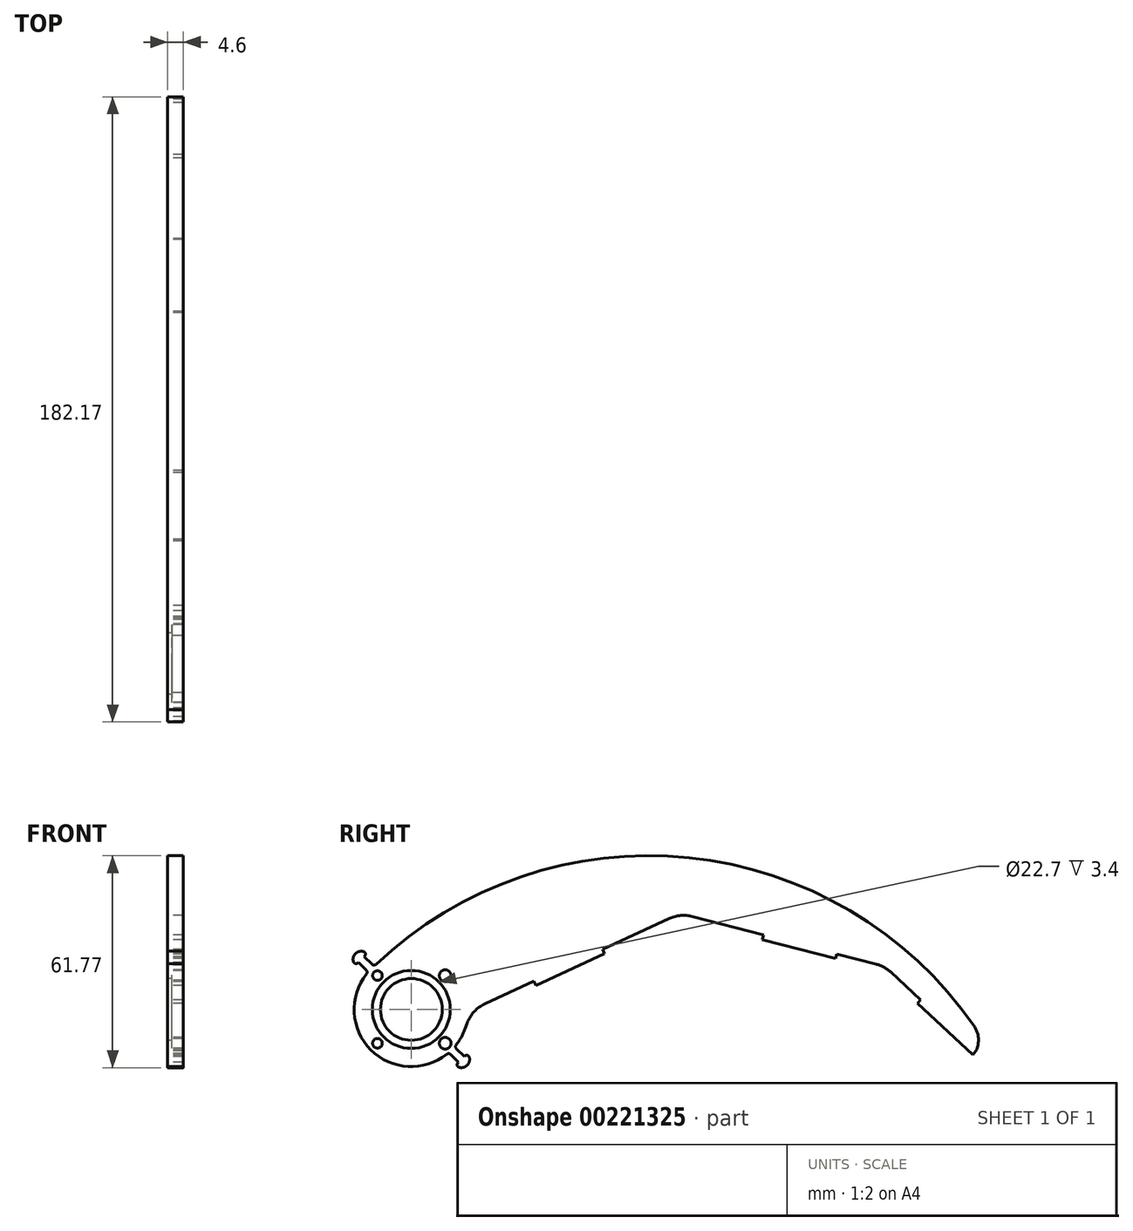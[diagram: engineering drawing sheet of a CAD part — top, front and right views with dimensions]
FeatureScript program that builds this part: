
annotation { "Feature Type Name" : "Feature", "Feature Type Description" : "" }
export const myFeature = defineFeature(function(context is Context, id is Id, definition is map)
    precondition{}
    {
        {
            var Q0;
            Q0=qCreatedBy(makeId("Right.planeOp"),FACE);
            var sketch = newSketch(context, id + "F0", { "sketchPlane" : qUnion([Q0])});
            skCircle(sketch, "E0", {"center": v(0, 0) * mm, "radius": 200 * mm, "construction": true});
            skCircle(sketch, "E1", {"center": v(0, 0) * mm, "radius": 9 * mm});
            skCircle(sketch, "E2", {"center": v(143.28, 0) * mm, "radius": 13 * mm, "construction": true});
            skCircle(sketch, "E3.1.0.0", {"center": v(200, 0) * mm, "radius": 200 * mm, "construction": true});
            skLineSegment(sketch, "E3.direction1", {"start": v(0, 0) * mm, "end": v(200, 0) * mm, "construction": true});
            skLineSegment(sketch, "E4", {"start": v(200, 0) * mm, "end": v(5.32, 45.84) * mm, "construction": true});
            skCircle(sketch, "E5", {"center": v(178.19, 0) * mm, "radius": 5 * mm, "construction": true});
            skCircle(sketch, "E6", {"center": v(108.38, 0) * mm, "radius": 21 * mm, "construction": true});
            skCircle(sketch, "E7", {"center": v(51.66, 0) * mm, "radius": 34 * mm, "construction": true});
            skCircle(sketch, "E8", {"center": v(0, 0) * mm, "radius": 13.95 * mm, "construction": true});
            skLineSegment(sketch, "E9", {"start": v(0, 0) * mm, "end": v(-9.86, 9.86) * mm, "construction": true});
            skCircle(sketch, "E10", {"center": v(-9.86, 9.86) * mm, "radius": 1.4 * mm});
            skCircle(sketch, "E11", {"center": v(0, 0) * mm, "radius": 11.25 * mm, "construction": true});
            skLineSegment(sketch, "E12", {"start": v(143.28, 0) * mm, "end": v(160.73, -17.45) * mm, "construction": true});
            skLineSegment(sketch, "E13", {"start": v(160.73, -17.45) * mm, "end": v(178.19, 0) * mm, "construction": true});
            skLineSegment(sketch, "E14", {"start": v(160.73, -17.45) * mm, "end": v(160.73, 0) * mm, "construction": true});
            skCircle(sketch, "E15.cCircle", {"center": v(88, -78.54) * mm, "radius": 100 * mm, "construction": true});
            skPoint(sketch, "E15.0.midPoint", {"position": v(88, 21.46) * mm});
            skLineSegment(sketch, "E16.bottom", {"start": v(56.28, 16.2) * mm, "end": v(36.32, 6.96) * mm});
            skLineSegment(sketch, "E16.top", {"start": v(55.7, 17.47) * mm, "end": v(35.73, 8.23) * mm, "construction": true});
            skLineSegment(sketch, "E16.left", {"start": v(56.28, 16.2) * mm, "end": v(55.7, 17.47) * mm});
            skLineSegment(sketch, "E16.right", {"start": v(36.32, 6.96) * mm, "end": v(35.73, 8.23) * mm});
            skPoint(sketch, "E16.middle", {"position": v(46, 12.22) * mm});
            skLineSegment(sketch, "E17", {"start": v(113.11, 18.26) * mm, "end": v(88, -78.54) * mm, "construction": true});
            skLineSegment(sketch, "E18", {"start": v(46, 12.22) * mm, "end": v(88, -78.54) * mm, "construction": true});
            skLineSegment(sketch, "E19.bottom", {"start": v(123.59, 14.82) * mm, "end": v(102.3, 20.34) * mm});
            skLineSegment(sketch, "E19.top", {"start": v(123.94, 16.17) * mm, "end": v(102.64, 21.7) * mm, "construction": true});
            skLineSegment(sketch, "E19.left", {"start": v(123.59, 14.82) * mm, "end": v(123.94, 16.17) * mm});
            skLineSegment(sketch, "E19.right", {"start": v(102.3, 20.34) * mm, "end": v(102.64, 21.7) * mm});
            skPoint(sketch, "E19.middle", {"position": v(113.11, 18.26) * mm});
            skLineSegment(sketch, "E20.bottom", {"start": v(164.5, -12.13) * mm, "end": v(163.54, -13.15) * mm});
            skLineSegment(sketch, "E20.top", {"start": v(148.35, 2.82) * mm, "end": v(147.4, 1.8) * mm});
            skLineSegment(sketch, "E20.left", {"start": v(164.5, -12.13) * mm, "end": v(148.35, 2.82) * mm, "construction": true});
            skLineSegment(sketch, "E20.right", {"start": v(163.54, -13.15) * mm, "end": v(147.4, 1.8) * mm});
            skPoint(sketch, "E20.middle", {"position": v(155.95, -5.17) * mm});
            skLineSegment(sketch, "E21", {"start": v(155.95, -5.17) * mm, "end": v(88, -78.54) * mm, "construction": true});
            skCircle(sketch, "E22", {"center": v(88, -78.54) * mm, "radius": 101.3 * mm, "construction": true});
            skCircle(sketch, "E23", {"center": v(160.83, -8.73) * mm, "radius": 5 * mm, "construction": true});
            skArc(sketch, "E24", {"start": v(163.89, -4.78) * mm, "mid": v(165.18, -8.37) * mm, "end": v(164.5, -12.13) * mm});
            skLineSegment(sketch, "E25", {"start": v(102.64, 21.7) * mm, "end": v(81.88, 27.09) * mm});
            skLineSegment(sketch, "E26", {"start": v(75.16, 26.48) * mm, "end": v(55.7, 17.47) * mm});
            skLineSegment(sketch, "E27", {"start": v(35.73, 8.23) * mm, "end": v(21.44, 1.62) * mm});
            skLineSegment(sketch, "E28", {"start": v(16.24, -4.05) * mm, "end": v(15.66, -5.66) * mm});
            skLineSegment(sketch, "E29", {"start": v(123.94, 16.17) * mm, "end": v(135.39, 13.2) * mm});
            skLineSegment(sketch, "E30", {"start": v(139.67, 10.86) * mm, "end": v(148.35, 2.82) * mm});
            skPoint(sketch, "E31.visualSharp", {"position": v(137.83, 12.57) * mm});
            skArc(sketch, "E31.filletArc", {"start": v(139.67, 10.86) * mm, "mid": v(137.68, 12.3) * mm, "end": v(135.39, 13.2) * mm});
            skPoint(sketch, "E32.visualSharp", {"position": v(78.41, 27.99) * mm});
            skArc(sketch, "E32.filletArc", {"start": v(81.88, 27.09) * mm, "mid": v(78.47, 27.37) * mm, "end": v(75.16, 26.48) * mm});
            skPoint(sketch, "E33.visualSharp", {"position": v(17.66, -0.13) * mm});
            skArc(sketch, "E33.filletArc", {"start": v(21.44, 1.62) * mm, "mid": v(18.27, -0.7) * mm, "end": v(16.24, -4.05) * mm});
            skCircle(sketch, "E34.1.0", {"center": v(-9.86, -9.86) * mm, "radius": 1.4 * mm});
            skCircle(sketch, "E34.2.0", {"center": v(9.86, -9.86) * mm, "radius": 1.4 * mm, "construction": true});
            skCircle(sketch, "E34.3.0", {"center": v(9.86, 9.86) * mm, "radius": 1.4 * mm, "construction": true});
            skCircle(sketch, "E35", {"center": v(0, 0) * mm, "radius": 21.25 * mm, "construction": true});
            skLineSegment(sketch, "E36", {"start": v(0, 0) * mm, "end": v(0, -17.25) * mm, "construction": true});
            skCircle(sketch, "E37", {"center": v(-9.86, -9.86) * mm, "radius": 2.7 * mm, "construction": true});
            skPoint(sketch, "E38.orphan", {"position": v(-2.72, -20.18) * mm});
            skCircle(sketch, "E39", {"center": v(9.86, 9.86) * mm, "radius": 1.7 * mm});
            skCircle(sketch, "E40", {"center": v(9.86, -9.86) * mm, "radius": 1.7 * mm});
            skArc(sketch, "E41", {"start": v(-12.6, 10.9) * mm, "mid": v(-11.77, -11.77) * mm, "end": v(10.9, -12.6) * mm});
            skLineSegment(sketch, "E42.bottom", {"start": v(-13.72, 15.42) * mm, "end": v(-10.9, 12.6) * mm});
            skLineSegment(sketch, "E42.top", {"start": v(-15.42, 13.72) * mm, "end": v(-12.6, 10.9) * mm});
            skLineSegment(sketch, "E42.left", {"start": v(-13.72, 15.42) * mm, "end": v(-15.42, 13.72) * mm, "construction": true});
            skLineSegment(sketch, "E43", {"start": v(-14.57, 14.57) * mm, "end": v(-11.74, 11.74) * mm, "construction": true});
            skArc(sketch, "E44", {"start": v(-12.87, 16.27) * mm, "mid": v(-16.27, 16.27) * mm, "end": v(-16.27, 12.87) * mm});
            skLineSegment(sketch, "E45", {"start": v(-13.72, 15.42) * mm, "end": v(-12.87, 16.27) * mm});
            skLineSegment(sketch, "E46", {"start": v(-15.42, 13.72) * mm, "end": v(-16.27, 12.87) * mm});
            skLineSegment(sketch, "E47", {"start": v(0, 0) * mm, "end": v(9.86, 9.86) * mm, "construction": true});
            skLineSegment(sketch, "E48.MirrorCS", {"start": v(15.42, -13.72) * mm, "end": v(12.6, -10.9) * mm});
            skLineSegment(sketch, "E49.MirrorCS", {"start": v(15.42, -13.72) * mm, "end": v(16.27, -12.87) * mm});
            skArc(sketch, "E50.MirrorCS", {"start": v(16.27, -12.87) * mm, "mid": v(16.27, -16.27) * mm, "end": v(12.87, -16.27) * mm});
            skLineSegment(sketch, "E51.MirrorCS", {"start": v(13.72, -15.42) * mm, "end": v(12.87, -16.27) * mm});
            skLineSegment(sketch, "E52.MirrorCS", {"start": v(13.72, -15.42) * mm, "end": v(10.9, -12.6) * mm});
            skArc(sketch, "E53.trimOffspring", {"start": v(12.6, -10.9) * mm, "mid": v(14.37, -8.42) * mm, "end": v(15.66, -5.66) * mm});
            skArc(sketch, "E54", {"start": v(163.89, -4.78) * mm, "mid": v(80.5, 44.24) * mm, "end": v(-10.9, 12.6) * mm});
            skLineSegment(sketch, "E55", {"start": v(0, 0) * mm, "end": v(26.66, -57.6) * mm, "construction": true});
            skLineSegment(sketch, "E56", {"start": v(0, 0) * mm, "end": v(-15.25, -58.78) * mm, "construction": true});
            skLineSegment(sketch, "E57", {"start": v(0, 0) * mm, "end": v(-37.75, -40.76) * mm, "construction": true});
            skSolve(sketch);
        }
        {
            var Q0;
            Q0 = qSketchRegion(id + "F0", true);
            extrude(context, id + "F1", {"entities" : qUnion([Q0]), "depth" : 1.2 * mm});
        }
        {
            var Q0;
            Q0=makeQuery(id+"F1.opExtrude","CAP_FACE",FACE,{"disambiguationData":[OSD([sQuery(id+"F0.wireOp",EDGE,"E1"),sQuery(id+"F0.wireOp",EDGE,"E10"),sQuery(id+"F0.wireOp",EDGE,"E16.bottom"),sQuery(id+"F0.wireOp",EDGE,"E16.left"),sQuery(id+"F0.wireOp",EDGE,"E16.right"),sQuery(id+"F0.wireOp",EDGE,"E19.bottom"),sQuery(id+"F0.wireOp",EDGE,"E19.left"),sQuery(id+"F0.wireOp",EDGE,"E19.right"),sQuery(id+"F0.wireOp",EDGE,"E20.bottom"),sQuery(id+"F0.wireOp",EDGE,"E20.top"),sQuery(id+"F0.wireOp",EDGE,"E20.right"),sQuery(id+"F0.wireOp",EDGE,"E24"),sQuery(id+"F0.wireOp",EDGE,"E25"),sQuery(id+"F0.wireOp",EDGE,"E26"),sQuery(id+"F0.wireOp",EDGE,"E27"),sQuery(id+"F0.wireOp",EDGE,"E28"),sQuery(id+"F0.wireOp",EDGE,"E29"),sQuery(id+"F0.wireOp",EDGE,"E30"),sQuery(id+"F0.wireOp",EDGE,"E31.filletArc"),sQuery(id+"F0.wireOp",EDGE,"E32.filletArc"),sQuery(id+"F0.wireOp",EDGE,"E33.filletArc"),sQuery(id+"F0.wireOp",EDGE,"E34.1.0"),sQuery(id+"F0.wireOp",EDGE,"E39"),sQuery(id+"F0.wireOp",EDGE,"E40"),sQuery(id+"F0.wireOp",EDGE,"E41"),sQuery(id+"F0.wireOp",EDGE,"E42.bottom"),sQuery(id+"F0.wireOp",EDGE,"E42.top"),sQuery(id+"F0.wireOp",EDGE,"E44"),sQuery(id+"F0.wireOp",EDGE,"E45"),sQuery(id+"F0.wireOp",EDGE,"E46"),sQuery(id+"F0.wireOp",EDGE,"E48.MirrorCS"),sQuery(id+"F0.wireOp",EDGE,"E49.MirrorCS"),sQuery(id+"F0.wireOp",EDGE,"E50.MirrorCS"),sQuery(id+"F0.wireOp",EDGE,"E51.MirrorCS"),sQuery(id+"F0.wireOp",EDGE,"E52.MirrorCS"),sQuery(id+"F0.wireOp",EDGE,"E53.trimOffspring"),sQuery(id+"F0.wireOp",EDGE,"E54")])],"isStart":false});
            var sketch = newSketch(context, id + "F2", { "sketchPlane" : qUnion([Q0])});
            skLineSegment(sketch, "E58.0", {"start": v(123.59, 14.82) * mm, "end": v(102.3, 20.34) * mm});
            skPoint(sketch, "E59.0", {"position": v(78.47, 27.37) * mm});
            skArc(sketch, "E59.1", {"start": v(81.88, 27.09) * mm, "mid": v(78.47, 27.37) * mm, "end": v(75.16, 26.48) * mm});
            skLineSegment(sketch, "E60.0", {"start": v(102.64, 21.7) * mm, "end": v(81.88, 27.09) * mm});
            skLineSegment(sketch, "E61.0", {"start": v(123.94, 16.17) * mm, "end": v(135.39, 13.2) * mm});
            skArc(sketch, "E62.0", {"start": v(139.67, 10.86) * mm, "mid": v(137.68, 12.3) * mm, "end": v(135.39, 13.2) * mm});
            skLineSegment(sketch, "E63.0", {"start": v(139.67, 10.86) * mm, "end": v(148.35, 2.82) * mm});
            skLineSegment(sketch, "E64.0", {"start": v(163.54, -13.15) * mm, "end": v(147.4, 1.8) * mm});
            skArc(sketch, "E65.0", {"start": v(163.89, -4.78) * mm, "mid": v(165.18, -8.37) * mm, "end": v(164.5, -12.13) * mm});
            skArc(sketch, "E66.0", {"start": v(163.89, -4.78) * mm, "mid": v(80.5, 44.24) * mm, "end": v(-10.9, 12.6) * mm});
            skLineSegment(sketch, "E67.0", {"start": v(75.16, 26.48) * mm, "end": v(55.7, 17.47) * mm});
            skLineSegment(sketch, "E68.0", {"start": v(56.28, 16.2) * mm, "end": v(36.32, 6.96) * mm});
            skArc(sketch, "E69.0", {"start": v(21.44, 1.62) * mm, "mid": v(18.27, -0.7) * mm, "end": v(16.24, -4.05) * mm});
            skLineSegment(sketch, "E70.0", {"start": v(16.24, -4.05) * mm, "end": v(15.66, -5.66) * mm});
            skArc(sketch, "E71.0", {"start": v(12.6, -10.9) * mm, "mid": v(14.37, -8.42) * mm, "end": v(15.66, -5.66) * mm});
            skLineSegment(sketch, "E72.0", {"start": v(15.42, -13.72) * mm, "end": v(12.6, -10.9) * mm});
            skLineSegment(sketch, "E73.0", {"start": v(13.72, -15.42) * mm, "end": v(10.9, -12.6) * mm});
            skCircle(sketch, "E74.0", {"center": v(9.86, -9.86) * mm, "radius": 1.7 * mm});
            skArc(sketch, "E75.0", {"start": v(-12.6, 10.9) * mm, "mid": v(-11.77, -11.77) * mm, "end": v(10.9, -12.6) * mm});
            skCircle(sketch, "E76.0", {"center": v(-9.86, -9.86) * mm, "radius": 1.4 * mm});
            skCircle(sketch, "E77.0", {"center": v(-9.86, 9.86) * mm, "radius": 1.4 * mm});
            skCircle(sketch, "E78.0", {"center": v(9.86, 9.86) * mm, "radius": 1.7 * mm});
            skLineSegment(sketch, "E79.0", {"start": v(-15.42, 13.72) * mm, "end": v(-12.6, 10.9) * mm});
            skLineSegment(sketch, "E80.0", {"start": v(-13.72, 15.42) * mm, "end": v(-10.9, 12.6) * mm});
            skArc(sketch, "E81.0", {"start": v(16.27, -12.87) * mm, "mid": v(16.27, -16.27) * mm, "end": v(12.87, -16.27) * mm});
            skArc(sketch, "E82.0", {"start": v(-12.87, 16.27) * mm, "mid": v(-16.27, 16.27) * mm, "end": v(-16.27, 12.87) * mm});
            skLineSegment(sketch, "E83", {"start": v(15.42, -13.72) * mm, "end": v(16.27, -12.87) * mm});
            skLineSegment(sketch, "E84", {"start": v(13.72, -15.42) * mm, "end": v(12.87, -16.27) * mm});
            skLineSegment(sketch, "E85", {"start": v(21.44, 1.62) * mm, "end": v(35.73, 8.23) * mm});
            skLineSegment(sketch, "E86", {"start": v(35.73, 8.23) * mm, "end": v(36.32, 6.96) * mm});
            skCircle(sketch, "E87", {"center": v(0, 0) * mm, "radius": 11.35 * mm});
            skLineSegment(sketch, "E88", {"start": v(-16.27, 12.87) * mm, "end": v(-15.42, 13.72) * mm});
            skLineSegment(sketch, "E89", {"start": v(-13.72, 15.42) * mm, "end": v(-12.87, 16.27) * mm});
            skLineSegment(sketch, "E90", {"start": v(55.7, 17.47) * mm, "end": v(56.28, 16.2) * mm});
            skLineSegment(sketch, "E91", {"start": v(102.64, 21.7) * mm, "end": v(102.3, 20.34) * mm});
            skLineSegment(sketch, "E92", {"start": v(123.59, 14.82) * mm, "end": v(123.94, 16.17) * mm});
            skLineSegment(sketch, "E93", {"start": v(148.35, 2.82) * mm, "end": v(147.4, 1.8) * mm});
            skLineSegment(sketch, "E94", {"start": v(163.54, -13.15) * mm, "end": v(164.5, -12.13) * mm});
            skCircle(sketch, "E95", {"center": v(0, 0) * mm, "radius": 9 * mm});
            skCircle(sketch, "E96", {"center": v(0, 0) * mm, "radius": 9.4 * mm});
            skSolve(sketch);
        }
        {
            var Q0;
            Q0 = qSketchRegion(id + "F2", true);
            extrude(context, id + "F3", {"entities" : qUnion([Q0]), "operationType" : NewBodyOperationType.ADD, "depth" : 3.4 * mm});
        }
        {
            var Q0;
            Q0=makeQuery(id+"F3.boolean.opBoolean","MERGE",EDGE,{"derivedFrom":[makeQuery(id+"F1.opExtrude","SWEPT_EDGE",EDGE,{"disambiguationData":[OSD([sQuery(id+"F0.wireOp",EDGE,"E50.MirrorCS"),sQuery(id+"F0.wireOp",EDGE,"E51.MirrorCS")])]}),makeQuery(id+"F3.opExtrude","SWEPT_EDGE",EDGE,{"disambiguationData":[OSD([sQuery(id+"F2.wireOp",EDGE,"E81.0"),sQuery(id+"F2.wireOp",EDGE,"E84")])]})]});
            var Q1;
            Q1=makeQuery(id+"F3.boolean.opBoolean","MERGE",EDGE,{"derivedFrom":[makeQuery(id+"F1.opExtrude","SWEPT_EDGE",EDGE,{"disambiguationData":[OSD([sQuery(id+"F0.wireOp",EDGE,"E44"),sQuery(id+"F0.wireOp",EDGE,"E46")])]}),makeQuery(id+"F3.opExtrude","SWEPT_EDGE",EDGE,{"disambiguationData":[OSD([sQuery(id+"F2.wireOp",EDGE,"E82.0"),sQuery(id+"F2.wireOp",EDGE,"E88")])]})]});
            var Q2;
            Q2=makeQuery(id+"F3.boolean.opBoolean","MERGE",EDGE,{"derivedFrom":[makeQuery(id+"F1.opExtrude","SWEPT_EDGE",EDGE,{"disambiguationData":[OSD([sQuery(id+"F0.wireOp",EDGE,"E44"),sQuery(id+"F0.wireOp",EDGE,"E45")])]}),makeQuery(id+"F3.opExtrude","SWEPT_EDGE",EDGE,{"disambiguationData":[OSD([sQuery(id+"F2.wireOp",EDGE,"E82.0"),sQuery(id+"F2.wireOp",EDGE,"E89")])]})]});
            var Q3;
            Q3=makeQuery(id+"F3.boolean.opBoolean","MERGE",EDGE,{"derivedFrom":[makeQuery(id+"F1.opExtrude","SWEPT_EDGE",EDGE,{"disambiguationData":[OSD([sQuery(id+"F0.wireOp",EDGE,"E41"),sQuery(id+"F0.wireOp",EDGE,"E52.MirrorCS")])]}),makeQuery(id+"F3.opExtrude","SWEPT_EDGE",EDGE,{"disambiguationData":[OSD([sQuery(id+"F2.wireOp",EDGE,"E73.0"),sQuery(id+"F2.wireOp",EDGE,"E75.0")])]})]});
            var Q4;
            Q4=makeQuery(id+"F3.boolean.opBoolean","MERGE",EDGE,{"derivedFrom":[makeQuery(id+"F1.opExtrude","SWEPT_EDGE",EDGE,{"disambiguationData":[OSD([sQuery(id+"F0.wireOp",EDGE,"E48.MirrorCS"),sQuery(id+"F0.wireOp",EDGE,"E53.trimOffspring")])]}),makeQuery(id+"F3.opExtrude","SWEPT_EDGE",EDGE,{"disambiguationData":[OSD([sQuery(id+"F2.wireOp",EDGE,"E71.0"),sQuery(id+"F2.wireOp",EDGE,"E72.0")])]})]});
            var Q5;
            Q5=makeQuery(id+"F3.boolean.opBoolean","MERGE",EDGE,{"derivedFrom":[makeQuery(id+"F1.opExtrude","SWEPT_EDGE",EDGE,{"disambiguationData":[OSD([sQuery(id+"F0.wireOp",EDGE,"E49.MirrorCS"),sQuery(id+"F0.wireOp",EDGE,"E50.MirrorCS")])]}),makeQuery(id+"F3.opExtrude","SWEPT_EDGE",EDGE,{"disambiguationData":[OSD([sQuery(id+"F2.wireOp",EDGE,"E81.0"),sQuery(id+"F2.wireOp",EDGE,"E83")])]})]});
            var Q6;
            Q6=makeQuery(id+"F3.boolean.opBoolean","MERGE",EDGE,{"derivedFrom":[makeQuery(id+"F1.opExtrude","SWEPT_EDGE",EDGE,{"disambiguationData":[OSD([sQuery(id+"F0.wireOp",EDGE,"E42.bottom"),sQuery(id+"F0.wireOp",EDGE,"E54")])]}),makeQuery(id+"F3.opExtrude","SWEPT_EDGE",EDGE,{"disambiguationData":[OSD([sQuery(id+"F2.wireOp",EDGE,"E66.0"),sQuery(id+"F2.wireOp",EDGE,"E80.0")])]})]});
            var Q7;
            Q7=makeQuery(id+"F3.boolean.opBoolean","MERGE",EDGE,{"derivedFrom":[makeQuery(id+"F1.opExtrude","SWEPT_EDGE",EDGE,{"disambiguationData":[OSD([sQuery(id+"F0.wireOp",EDGE,"E41"),sQuery(id+"F0.wireOp",EDGE,"E42.top")])]}),makeQuery(id+"F3.opExtrude","SWEPT_EDGE",EDGE,{"disambiguationData":[OSD([sQuery(id+"F2.wireOp",EDGE,"E75.0"),sQuery(id+"F2.wireOp",EDGE,"E79.0")])]})]});
            fillet(context, id + "F4", {"entities" : qUnion([Q0, Q1, Q2, Q3, Q4, Q5, Q6, Q7]), "radius" : 0.8 * mm, "allowEdgeOverflow" : false});
        }
    });
